# Revit family: BuzziJet
name_source: partatom
category: Lighting Fixtures
revit_build: Autodesk Revit 2017 (Build: 20170816_0615(x64)
units: mm (PartAtom-declared; Revit-internal decimal feet)

## family parameters
Always vertical = Yes
Cut with Voids When Loaded = No
Host = Ceiling
Light Source = Yes
OmniClass Number = 23.80.70.11
OmniClass Title = Luminaries for Internal Lighting
Part Type = Normal
Room Calculation Point = No
Round Connector Dimension = Use Diameter
Shared = No

## types (4) — shared parameters
Color Filter = 16777215
Cord Material = <By Category>
Dimming Lamp Color Temperature Shift = <None>
Frame Material = <By Category>
Lens Material = <By Category>
Light Source Symbol Size = 2' - 0"
Shade Material = <By Category>

## per-type parameters (varying)
| type | Shade Height | Split | Straight |
| BuzziJet S Straight | 0' - 8 7/8" | No | Yes |
| BuzziJet M Straight | 1' - 5 23/32" | No | Yes |
| BuzziJet S Split | 0' - 8 7/8" | Yes | No |
| BuzziJet M Split | 1' - 5 23/32" | Yes | No |

## geometry (parser evidence)
native form markers: Sweep x6
no freeform markers — native parametric forms only
